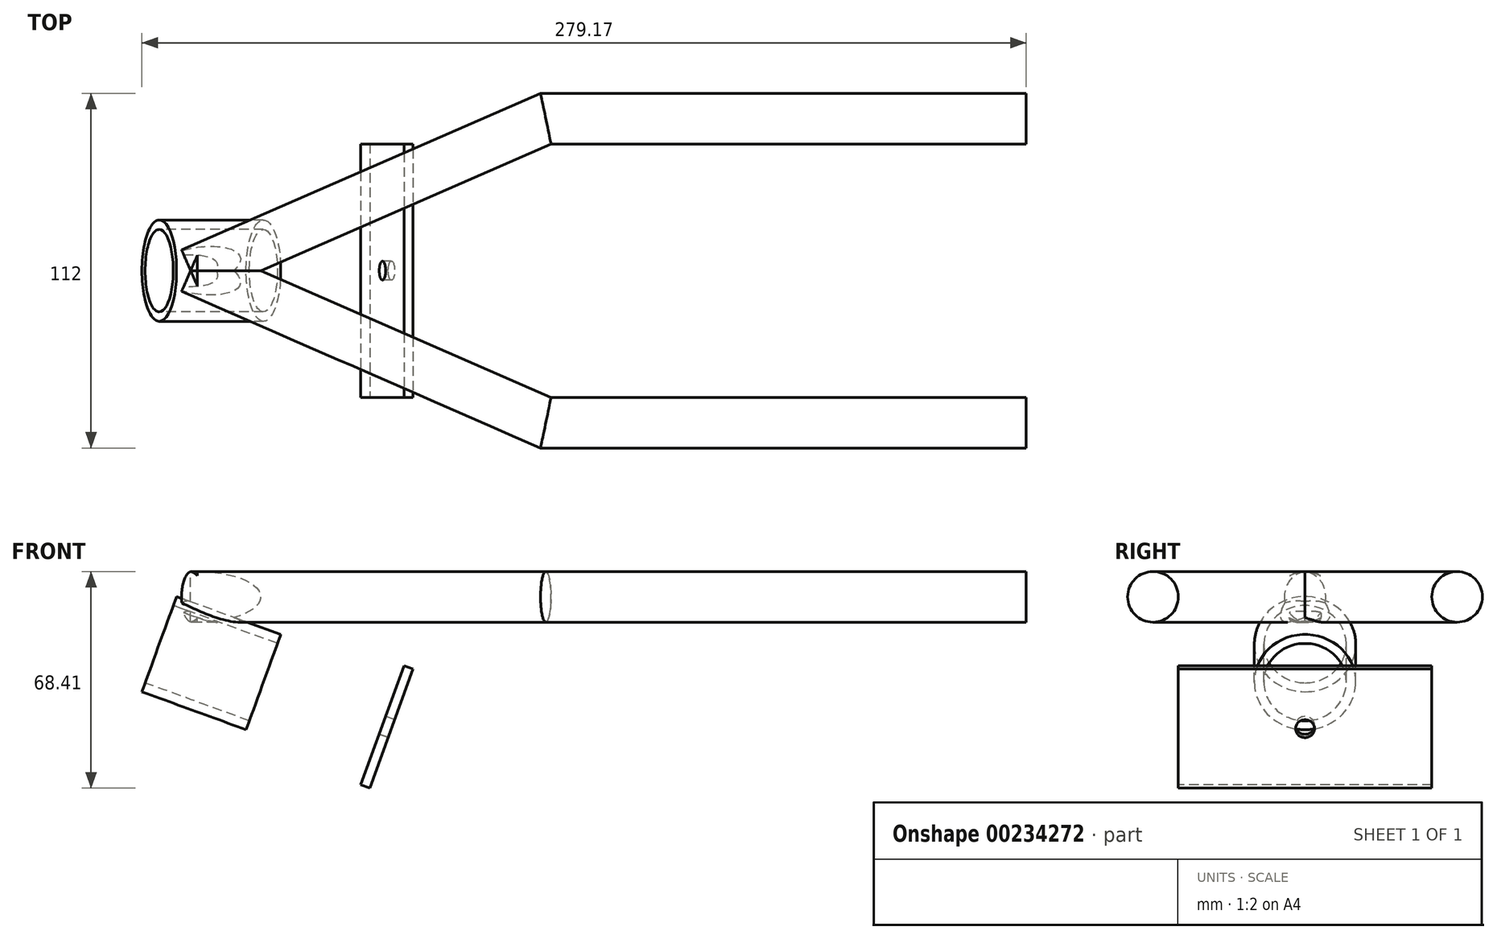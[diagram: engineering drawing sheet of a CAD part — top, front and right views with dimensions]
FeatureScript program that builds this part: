
annotation { "Feature Type Name" : "Feature", "Feature Type Description" : "" }
export const myFeature = defineFeature(function(context is Context, id is Id, definition is map)
    precondition{}
    {
        {
            var Q0;
            Q0=qCreatedBy(makeId("Top.planeOp"),FACE);
            var sketch = newSketch(context, id + "F0", { "sketchPlane" : qUnion([Q0])});
            skLineSegment(sketch, "E0", {"start": v(63, 0) * mm, "end": v(0, 0) * mm, "construction": true});
            skLineSegment(sketch, "E1", {"start": v(0, 40) * mm, "end": v(150, 40) * mm});
            skLineSegment(sketch, "E2", {"start": v(0, 40) * mm, "end": v(-91.65, 0) * mm});
            skLineSegment(sketch, "E3", {"start": v(-3.34, 56) * mm, "end": v(-108.74, 10) * mm});
            skLineSegment(sketch, "E4", {"start": v(-3.34, 56) * mm, "end": v(150, 56) * mm});
            skLineSegment(sketch, "E5", {"start": v(150, 40) * mm, "end": v(150, 56) * mm, "construction": true});
            skLineSegment(sketch, "E6", {"start": v(-113.44, -0.78) * mm, "end": v(-1.67, 48) * mm});
            skLineSegment(sketch, "E7", {"start": v(-1.67, 48) * mm, "end": v(150, 48) * mm});
            skLineSegment(sketch, "E8.MirrorCS", {"start": v(0, -40) * mm, "end": v(-91.65, 0) * mm});
            skLineSegment(sketch, "E9.MirrorCS", {"start": v(-3.34, -56) * mm, "end": v(-108.74, -10) * mm});
            skLineSegment(sketch, "E10.MirrorCS", {"start": v(-3.34, -56) * mm, "end": v(150, -56) * mm});
            skLineSegment(sketch, "E11.MirrorCS", {"start": v(0, -40) * mm, "end": v(150, -40) * mm});
            skLineSegment(sketch, "E12.MirrorCS", {"start": v(150, -40) * mm, "end": v(150, -56) * mm, "construction": true});
            skLineSegment(sketch, "E13.MirrorCS", {"start": v(-1.67, -48) * mm, "end": v(150, -48) * mm});
            skLineSegment(sketch, "E14.MirrorCS", {"start": v(-113.44, 0.78) * mm, "end": v(-1.67, -48) * mm});
            skLineSegment(sketch, "E15", {"start": v(-108.74, 10) * mm, "end": v(-108.74, -10) * mm, "construction": true});
            skSolve(sketch);
        }
        {
            var Q0;
            Q0=sQuery(id+"F0.wireOp",VERTEX,"E13.MirrorCS.end");
            var Q1;
            Q1=sQuery(id+"F0.wireOp",EDGE,"E13.MirrorCS");
            cPlane(context, id + "F1", {"entities" : qUnion([Q0, Q1]), "cplaneType" : CPlaneType.LINE_POINT, "offset" : 25 * mm, "width" : 150 * mm, "height" : 150 * mm});
        }
        {
            var Q0;
            Q0=qCreatedBy(id+"F1.planeOp",FACE);
            var sketch = newSketch(context, id + "F2", { "sketchPlane" : qUnion([Q0])});
            skPoint(sketch, "E16.0", {"position": v(-48, 0) * mm});
            skPoint(sketch, "E17.0", {"position": v(48, 0) * mm});
            skCircle(sketch, "E18", {"center": v(-48, 0) * mm, "radius": 8 * mm});
            skCircle(sketch, "E19", {"center": v(48, 0) * mm, "radius": 8 * mm});
            skSolve(sketch);
        }
        {
            var Q0;
            Q0=makeQuery(id+"F2.imprint","IMPRINT",FACE,{"disambiguationData":[TD([[makeQuery(id+"F2.imprint","IMPRINT",EDGE,{"derivedFrom":sQuery(id+"F2.wireOp",EDGE,"E18")}),1.0]])]});
            var Q1;
            Q1=sQuery(id+"F0.wireOp",EDGE,"E13.MirrorCS");
            var Q2;
            Q2=sQuery(id+"F0.wireOp",EDGE,"E14.MirrorCS");
            sweep(context, id + "F3", {"profiles" : qUnion([Q0]), "path" : qUnion([Q1, Q2])});
        }
        {
            var Q0;
            Q0=makeQuery(id+"F2.imprint","IMPRINT",FACE,{"disambiguationData":[TD([[makeQuery(id+"F2.imprint","IMPRINT",EDGE,{"derivedFrom":sQuery(id+"F2.wireOp",EDGE,"E19")}),1.0]])]});
            var Q1;
            Q1=sQuery(id+"F0.wireOp",EDGE,"E7");
            var Q2;
            Q2=sQuery(id+"F0.wireOp",EDGE,"E6");
            sweep(context, id + "F4", {"operationType" : NewBodyOperationType.ADD, "profiles" : qUnion([Q0]), "path" : qUnion([Q1, Q2])});
        }
        {
            assignVariable(context, id + "F5", {"name" : "LenInel", "anyValue" : 35});
        }
        {
            var Q0;
            Q0=qCreatedBy(makeId("Front.planeOp"),FACE);
            var sketch = newSketch(context, id + "F6", { "sketchPlane" : qUnion([Q0])});
            skPoint(sketch, "E20.0", {"position": v(-91.65, 0) * mm});
            skLineSegment(sketch, "E21.0", {"start": v(63, 0) * mm, "end": v(0, 0) * mm});
            skLineSegment(sketch, "E22", {"start": v(-123.7, -14.94) * mm, "end": v(-90.8, -26.91) * mm});
            skLineSegment(sketch, "E23", {"start": v(-91.65, 0) * mm, "end": v(-100.2, -23.5) * mm, "construction": true});
            skSolve(sketch);
        }
        {
            var Q0;
            Q0=sQuery(id+"F6.wireOp",VERTEX,"E22.start");
            var Q1;
            Q1=sQuery(id+"F6.wireOp",EDGE,"E22");
            cPlane(context, id + "F7", {"entities" : qUnion([Q0, Q1]), "cplaneType" : CPlaneType.LINE_POINT, "offset" : 25 * mm, "width" : 150 * mm, "height" : 150 * mm});
        }
        {
            var Q0;
            Q0=qCreatedBy(id+"F7.planeOp",FACE);
            var sketch = newSketch(context, id + "F8", { "sketchPlane" : qUnion([Q0])});
            skPoint(sketch, "E24.0", {"position": v(0, -56.35) * mm});
            skCircle(sketch, "E25", {"center": v(0, -56.35) * mm, "radius": 16 * mm});
            skCircle(sketch, "E26", {"center": v(0, -56.35) * mm, "radius": 13 * mm});
            skSolve(sketch);
        }
        {
            var Q0;
            Q0=makeQuery(id+"F8.imprint","IMPRINT",FACE,{"disambiguationData":[TD([[makeQuery(id+"F8.imprint","IMPRINT",EDGE,{"derivedFrom":sQuery(id+"F8.wireOp",EDGE,"E25")}),1.0]])]});
            extrude(context, id + "F9", {"entities" : qUnion([Q0]), "depth" : (getVariable(context, 'LenInel')) * mm});
        }
        {
            assignVariable(context, id + "F10", {"name" : "DstBasePot", "anyValue" : 40});
        }
        {
            var Q0;
            Q0=makeQuery(id+"F9.opExtrude","CAP_FACE",FACE,{"disambiguationData":[OSD([sQuery(id+"F8.wireOp",EDGE,"E25"),sQuery(id+"F8.wireOp",EDGE,"E26")])],"isStart":false});
            cPlane(context, id + "F11", {"entities" : qUnion([Q0]), "cplaneType" : CPlaneType.OFFSET, "offset" : (getVariable(context, 'DstBasePot')) * mm, "width" : 150 * mm, "height" : 150 * mm});
        }
        {
            var Q0;
            Q0=qCreatedBy(id+"F11.planeOp",FACE);
            var sketch = newSketch(context, id + "F12", { "sketchPlane" : qUnion([Q0])});
            skPoint(sketch, "E27.0", {"position": v(0, -56.35) * mm});
            skCircle(sketch, "E28", {"center": v(0, -56.35) * mm, "radius": 3 * mm});
            skLineSegment(sketch, "E29.bottom", {"start": v(40, -76.35) * mm, "end": v(-40, -76.35) * mm});
            skLineSegment(sketch, "E29.top", {"start": v(40, -36.35) * mm, "end": v(-40, -36.35) * mm});
            skLineSegment(sketch, "E29.left", {"start": v(40, -76.35) * mm, "end": v(40, -36.35) * mm});
            skLineSegment(sketch, "E29.right", {"start": v(-40, -76.35) * mm, "end": v(-40, -36.35) * mm});
            skSolve(sketch);
        }
        {
            var Q0;
            Q0=makeQuery(id+"F12.imprint","IMPRINT",FACE,{"disambiguationData":[TD([[makeQuery(id+"F12.imprint","IMPRINT",EDGE,{"derivedFrom":sQuery(id+"F12.wireOp",EDGE,"E28")}),-1.0]])]});
            extrude(context, id + "F13", {"entities" : qUnion([Q0]), "depth" : 3 * mm});
        }
    });
